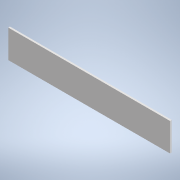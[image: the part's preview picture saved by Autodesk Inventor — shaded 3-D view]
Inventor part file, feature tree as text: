
AUTODESK INVENTOR PART (.ipt)
format: ipt  version: 2020 (Build 240168000, 168)  size: 91,136 bytes
history: native  units: in
note: dims shown in document units (in); Inventor stores cm internally (conversion verified against a paired STEP export)
features: extrude x1, sketch x1
ambient origin geometry x8: Origin, YZ Plane, XZ Plane, XY Plane, X Axis, Y Axis, Z Axis, Center Point
bodies: Solid1 (feature_tree)
feature tree (2):
  extrude  "Extrusion1"  Depth=23.0in
  sketch  "Sketch1"  dims[d0=4.0in d1=23.0in d2=0.25in d3=0.0in]
